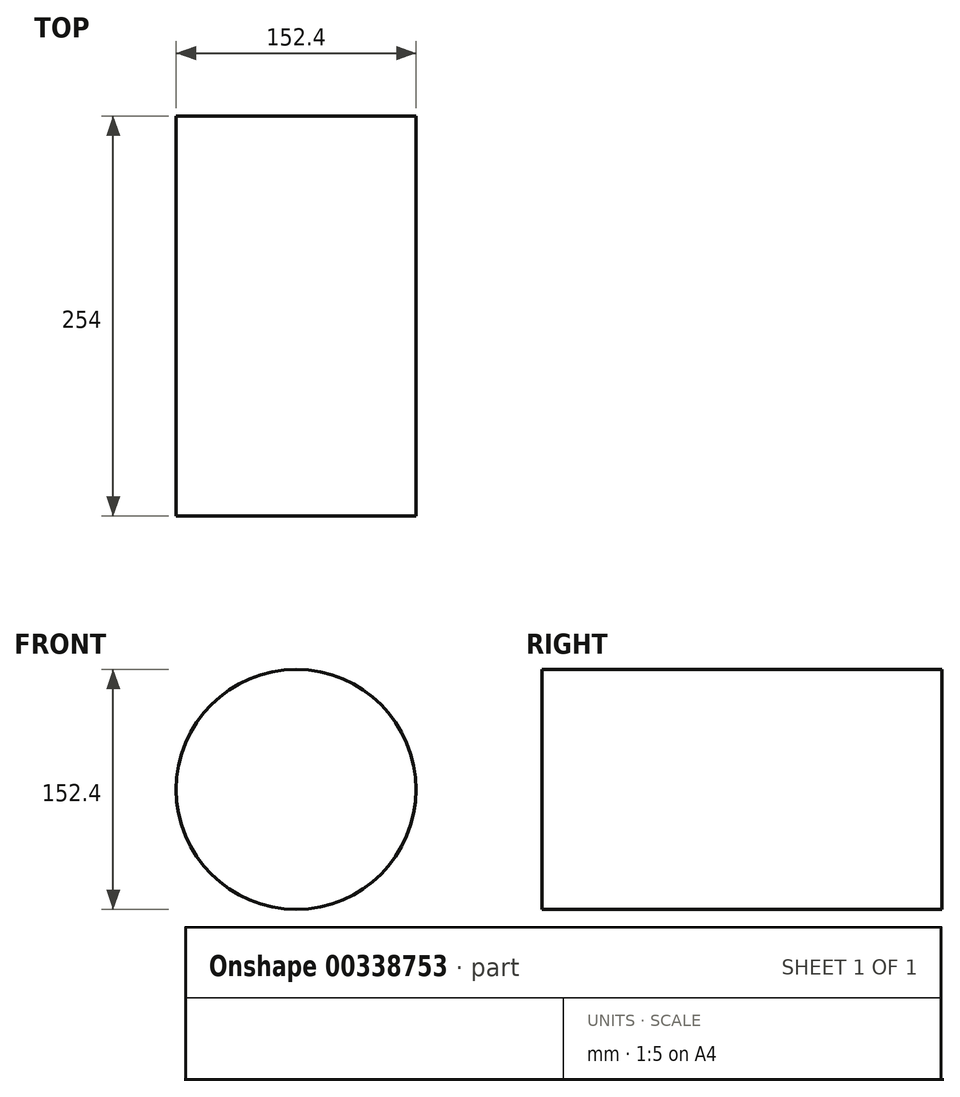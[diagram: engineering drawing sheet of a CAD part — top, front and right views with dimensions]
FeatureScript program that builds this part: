
annotation { "Feature Type Name" : "Feature", "Feature Type Description" : "" }
export const myFeature = defineFeature(function(context is Context, id is Id, definition is map)
    precondition{}
    {
        {
            var Q0;
            Q0=qCreatedBy(makeId("Front.planeOp"),FACE);
            var sketch = newSketch(context, id + "F0", { "sketchPlane" : qUnion([Q0])});
            skCircle(sketch, "E0", {"center": v(0, 0) * mm, "radius": 76.2 * mm});
            skSolve(sketch);
        }
        {
            var Q0;
            Q0=makeQuery(id+"F0.imprint","IMPRINT",FACE,{"disambiguationData":[TD([[makeQuery(id+"F0.imprint","IMPRINT",EDGE,{"derivedFrom":sQuery(id+"F0.wireOp",EDGE,"E0")}),1.0]])]});
            extrude(context, id + "F1", {"entities" : qUnion([Q0]), "endBound" : BoundingType.SYMMETRIC, "depth" : 254 * mm});
        }
    });
